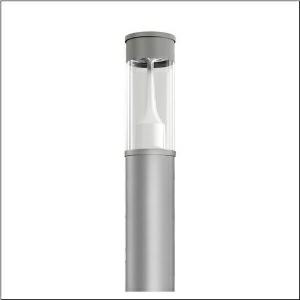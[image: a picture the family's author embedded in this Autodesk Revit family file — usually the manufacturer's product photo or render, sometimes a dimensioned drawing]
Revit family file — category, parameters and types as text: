
# Revit family: city-light_400_iq___st1_2a_5xa5305af14hp_8cfd
name_source: partatom
category: Lighting Fixtures
units: mm (PartAtom-declared; Revit-internal decimal feet)

## family parameters
Cut with Voids When Loaded = No
Host = Face
Light Source = No
Part Type = Normal
Room Calculation Point = No
Round Connector Dimension = Use Diameter
Shared = No

## types (1)
- --- (1 x LED, 3910 lm, 33.6 W, 2200K)
    Apparent Load = 34 VA
    CIE Flux Codes = 22 61 94 96 100
    Color Rendering = 70
    Color Temperature = 2200K
    Default Elevation = 1800 mm
    Description = City-Light 400 iQ, light pillar, Module 540 iQ-SR, primary light control with 3 zone facetted reflector, of plastic, silver coated, highly specular, structured, primary optical cover: cover, of PMMA, transparent, partly coated, light distribution: ST1.2a, primary light characteristic: asymmetric, LED, High Power LED, rated luminous flux: 3.910lm, luminous efficacy: 116lm/W, light colour: 722, colour temperature: 2200K, control gear: iQ Street-Remote, control: pre-setting: logarithmic dimming characteristic, Street-Remote, Auto-Match, Temp-Guard, Lumen-Switch, Night-Set, Smart-Wire, Light-Fading, Desk-Remote (wireless, voltage-free reading and setting of iQ features in the workshop via application-optimized NFC function/RFID function), optimised constant luminous flux control (CLO 2.0), with terminal, 6-pole, max. 2.5mm², mains connection: 230..240V, AC, 50/60Hz, start of lifetime: 34W, end of service life: 36W, reduction: 15W, luminaire housing, cylindrical, of extruded aluminium section, coated, Siteco® metallic grey (DB 702S), length: 4.694mm, diameter: 200mm, Module 540 iQ-SR, traffic white (RAL 9016), equipment: Power, protection rating (complete): IP65, insulation class (complete): insulation class II (safety insulation), certification: CE, ENEC, VDE, packaging unit: 1 piece

Light Distribution: ST1.2a
    Height = 500 mm
    Lamp = 1 x LED
    Lamp Light Flux = 3910 lm
    Lamp Power = 33.6 W
    Lamp count = 1
    Length = 200 mm  [stored 0.656168 ft]
    Luminous efficacy = 116 lm/W
    Manufacturer = Siteco
    ModVariant = No
    Model = 5XA5305AF14HP
    Mounting Place = Floor
    Mounting Type = Freestanding
    Number of Poles = 1
    OnlyDefault = Yes
    Power Factor = 1
    Product Name = City-Light 400 iQ | ST1.2a
    Product group = light pillar
    ProductGroupID = 1301
    Protection Class = Protection class II
    Protection Degree = IP 65
    RLX_Detail_Level = 1
    RLX_Emergency_Light_Flux = 0 lm
    RLX_Emergency_Type = 0
    RLX_Emergency_Type_DB = No
    RlxData = <blob elided: 53317 chars, md5=16185daf>
    Socket = socket
    Standby Power = 0 W
    System Light Flux = 3910 lm
    System Power = 34 W
    Type Comments = factory setting: luminous flux: 100 % | dim-lin: 254 | 695 mA
    Type Image = l_1006916.jpg
    URL = http://relux.com
    VarID = @adj_192898
    Voltage = 0 V
    Weight = 0.00 kg
    Width = 0 mm  [stored 0 ft]

note: [stored X ft] marks values corroborated as IEEE doubles in the binary element streams (Revit-internal decimal feet)

## geometry (parser evidence)
native form markers: Blend x4, Sweep x9
no freeform markers — native parametric forms only
